# Revit family: Hager-MINIGAMMA-Surface_mounted-IP30-Without_Cover-Without_DIN-Hosted-ES-es
name_source: partatom
category: Electrical Equipment
units: mm (PartAtom-declared; Revit-internal decimal feet)

## family parameters
Cut with Voids When Loaded = No
Host = Face
Maintain Annotation Orientation = Yes
Panel Configuration = Two Columns, Circuits Across
Part Type = Panelboard
Room Calculation Point = No
Round Connector Dimension = Use Diameter
Shared = No

## types (3) — shared parameters
BC_MODEL_ID = 1554399
BC_OBJECT_ID = 513901
BC_OBJECT_VERSION = #5
Code hager = ADD-EC000214_EU
EF000003 - Método de montaje = Montado superficial (escayola)
EF000007 - Color = Blanco
EF000024 - Resistente a UV = No
EF000049 - Profundidad = 82 mm  [stored 0.269029 ft]
EF000116 - Número RAL = 9010
EF000118 - Con placa de montaje = No
EF000266 - Número de filas = 1
EF001062 - Versión de CEM = No
EF001134 - Carril DIN = No
EF004462 - Tipo de cierre = Otros
EF005474 - Grado de protección (IP) = IP30
EF006244 - Tapa/puerta transparente = No
EF006306 - Con candado = No
EF009212 - Versión de la cubierta = Con muesca
EF015776 - Borne de tierra = No
EF015777 - Borne neutro = No
EF015941 - Puerta de transmisión de señal = No
ETIM class code = EC000214
ETIM class name = Small distribution board
HG000001 - Número de columnas = 1
HG000002-with door or cover-es = No
HG000003-Range-es = MINIGAMMA
HG000005-Thickness-es = 2 mm  [stored 0.00656168 ft]
HG000006-Flush mounted-es = No
HG000009-Double swing door-es = No
HG000010-Asymmetric doors-es = No
HG000011-Empty rows from bottom-es = No
HG000012-Door swing angle-es = 90.00°
HG000013-Door on the left-es = No
HG000014-Door on the right-es = Yes
HG000015-Clearance visibility-es = Yes
HG000016-Door 3D visibility-es = Yes
HG000017-Distance between poles-es = 18 mm  [stored 0.0590551 ft]
HG000060-RAL-number = 9010
HG000099-Onfly Template ID-es-ES = 507532
HGEF000266-Número de filas = 1
Manufacturer = Hager
Name = MINIGAMMA-Surface_mounted-IP30-Without_Cover-Without_DIN-ES
Name BIM&CO = Electricity
Name hager = ADD_Enclosures_EC000214
Uniformat = Low Tension Service & Dist.
Uniformat code = D501001
zero-valued in all types: Default Elevation, EF000218 - Profundidad de instalación, EF000332 - Altura de la instalación, EF000846 - Anchura de montaje, EF001131 - Profundidad interna, HG000007-Number of empty columns-es, HG000008-Number of empty rows-es

## per-type parameters (varying)
| type | BC_VARIANT_ID | EF000008 - Anchura | EF000040 - Altura | EF001088 - Posibilidad de extensión | EF002950 - Ancho en número de espacios modulares | HG000004-Manufacturer reference-es | HGEF0002950-Ancho en número de espacios modulares |
| MINIGAMMA-Surface_mounted_W55_H160_D82_2_Modular_Spacing-GD102B | 1179042 | 55 mm  [stored 0.180446 ft] | 160 mm  [stored 0.524934 ft] | No | 2 | GD102B | 2 |
| MINIGAMMA-Surface_mounted_W110_H180_D82_4_Modular_Spacing-GD104B | 1179043 | 110 mm  [stored 0.360892 ft] | 180 mm  [stored 0.590551 ft] | No | 4 | GD104B | 4 |
| MINIGAMMA-Surface_mounted_W146_H180_D82_6_Modular_Spacing-GD106B | 1179044 | 146 mm  [stored 0.479003 ft] | 180 mm  [stored 0.590551 ft] | Yes | 6 | GD106B | 6 |

note: column(s) folded — value = type name in every type: Reference

note: [stored X ft] marks values corroborated as IEEE doubles in the binary element streams (Revit-internal decimal feet)

## geometry (parser evidence)
native form markers: Sweep x14
no freeform markers — native parametric forms only
